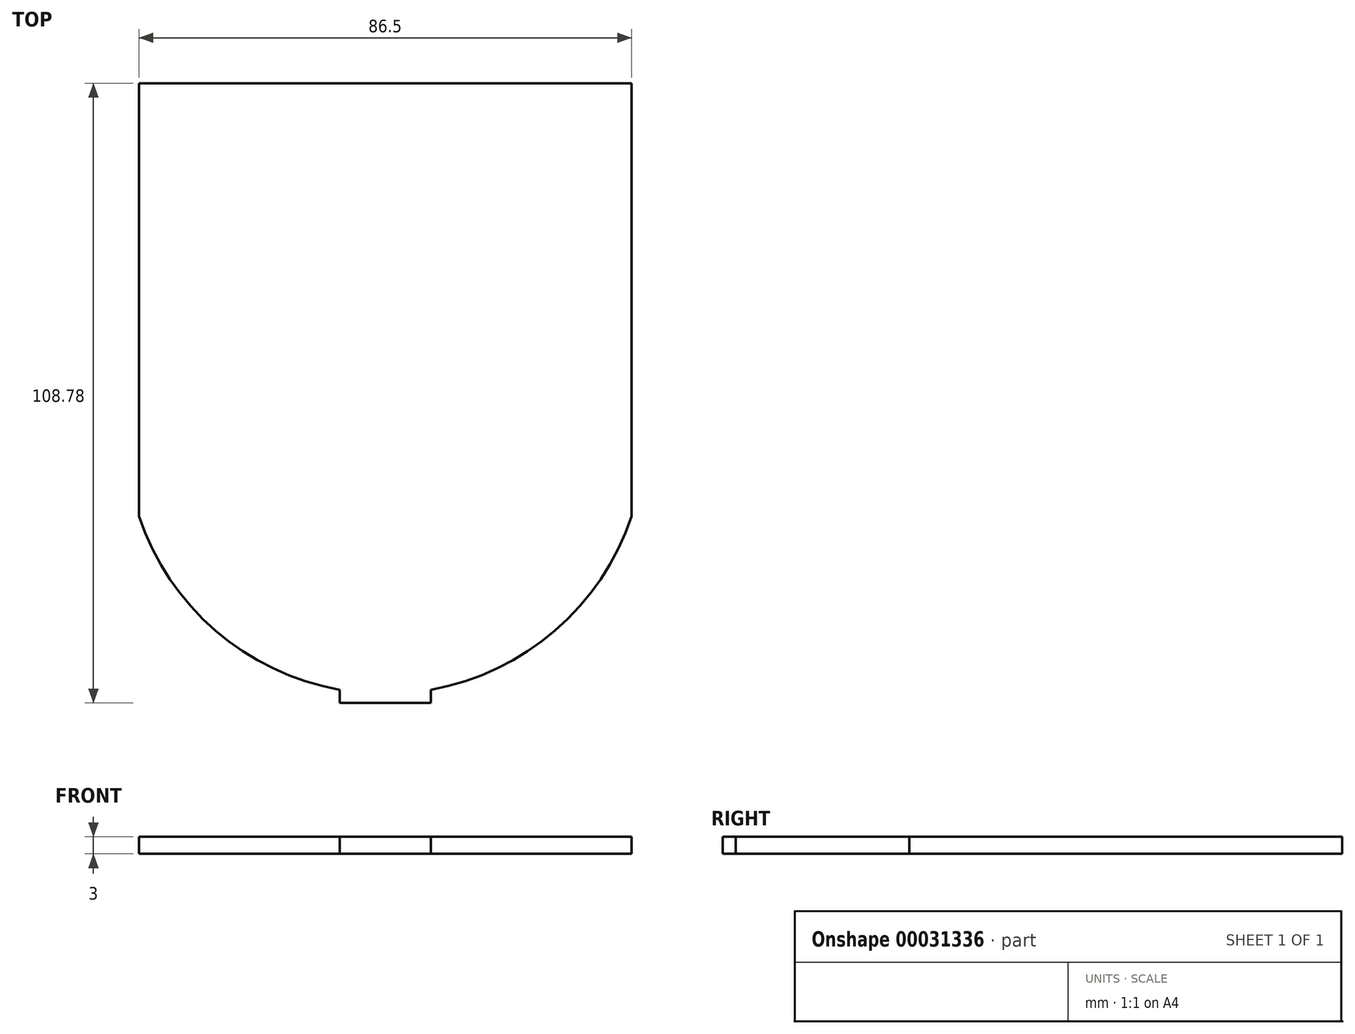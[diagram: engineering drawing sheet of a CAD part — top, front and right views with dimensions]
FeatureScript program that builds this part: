
annotation { "Feature Type Name" : "Feature", "Feature Type Description" : "" }
export const myFeature = defineFeature(function(context is Context, id is Id, definition is map)
    precondition{}
    {
        {
            var Q0;
            Q0=qCreatedBy(makeId("Top.planeOp"),FACE);
            var sketch = newSketch(context, id + "F0", { "sketchPlane" : qUnion([Q0])});
            skLineSegment(sketch, "E0.bottom", {"start": v(-41.08, 29.97) * mm, "end": v(45.42, 29.97) * mm});
            skLineSegment(sketch, "E0.top", {"start": v(-41.08, -46.03) * mm, "end": v(45.42, -46.03) * mm});
            skLineSegment(sketch, "E0.left", {"start": v(-41.08, 29.97) * mm, "end": v(-41.08, -46.03) * mm});
            skLineSegment(sketch, "E0.right", {"start": v(45.42, 29.97) * mm, "end": v(45.42, -46.03) * mm});
            skArc(sketch, "E1", {"start": v(-41.08, -46.03) * mm, "mid": v(2.17, -77.2) * mm, "end": v(45.42, -46.03) * mm});
            skLineSegment(sketch, "E2", {"start": v(2.17, -46.03) * mm, "end": v(2.17, -77.2) * mm});
            skLineSegment(sketch, "E3.top", {"start": v(-5.83, -78.8) * mm, "end": v(2.17, -78.8) * mm});
            skLineSegment(sketch, "E3.left", {"start": v(-5.83, -76.5) * mm, "end": v(-5.83, -78.8) * mm});
            skLineSegment(sketch, "E4.bottom", {"start": v(2.17, -78.8) * mm, "end": v(10.17, -78.8) * mm});
            skLineSegment(sketch, "E4.right", {"start": v(10.17, -78.8) * mm, "end": v(10.17, -76.5) * mm});
            skSolve(sketch);
        }
        {
            var Q0;
            {var subQ0=sQuery(id+"F0.wireOp",EDGE,"E2");Q0=makeQuery(id+"F0.imprint","IMPRINT",FACE,{"disambiguationData":[TD([[makeQuery(id+"F0.imprint","IMPRINT",EDGE,{"derivedFrom":subQ0}),-1.0]])]});}
            var Q1;
            {var subQ0=sQuery(id+"F0.wireOp",EDGE,"E2");Q1=makeQuery(id+"F0.imprint","IMPRINT",FACE,{"disambiguationData":[TD([[makeQuery(id+"F0.imprint","IMPRINT",EDGE,{"derivedFrom":subQ0}),1.0]])]});}
            var Q2;
            Q2=makeQuery(id+"F0.imprint","IMPRINT",FACE,{"disambiguationData":[TD([[makeQuery(id+"F0.imprint","IMPRINT",EDGE,{"derivedFrom":sQuery(id+"F0.wireOp",EDGE,"E0.bottom")}),-1.0]])]});
            var Q3;
            Q3=makeQuery(id+"F0.imprint","IMPRINT",FACE,{"disambiguationData":[TD([[makeQuery(id+"F0.imprint","IMPRINT",EDGE,{"derivedFrom":sQuery(id+"F0.wireOp",EDGE,"E3.top")}),1.0]])]});
            extrude(context, id + "F1", {"entities" : qUnion([Q0, Q1, Q2, Q3]), "depth" : 3 * mm});
        }
    });
